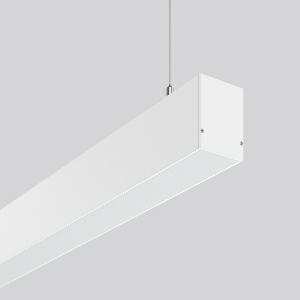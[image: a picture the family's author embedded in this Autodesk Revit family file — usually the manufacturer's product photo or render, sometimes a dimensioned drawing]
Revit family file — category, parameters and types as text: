
# Revit family: less_is_more_50_312318_002_21ed
name_source: partatom
category: Lighting Fixtures
units: mm (PartAtom-declared; Revit-internal decimal feet)

## family parameters
Cut with Voids When Loaded = No
Host = Face
Light Source = No
Part Type = Normal
Room Calculation Point = No
Round Connector Dimension = Use Diameter
Shared = No

## types (1)
- LESS IS MORE 50 (1 x LED Modul 830, 4600 lm, 3000)
    Apparent Load = 40 VA
    CIE Flux Codes = 49 80 96 63 100
    Color Rendering = 80
    Color Temperature = 3000
    Default Elevation = 1800 mm
    Description = Series: LESS IS MORE 50
Linear pendant luminaire for aesthetically sophisticated lighting. Housing: extruded aluminium profile, powder-coated. End cap aluminium powder-coated. Canopy made of aluminium, powder-coated. Diffuser made of non-yellowing plastic (PMMA), opal. Direct 65%, indirect 35% light emission. Suitable for pendant. 2-point steel cable suspension freely positionable and infinitely height-adjustable. Special lengths available on request. LED unit with integrated converter interchangeable and removable. Suitable for through-wiring. With sensors or as a safety luminaire on request. 
Colour: traffic white, matt (RAL 9016)
Length: 1127 mm
Width: 57 mm
Height: 75 mm
Suspension length: 2000 mm
Lamp: LED
Socket: without socket
Colour temperature: 3000K
Colour rendering index (CRI): 80
Light source: LED
Socket lamp2: Without base
Colour temperature: 3000K
System power: 40 W
Rated luminous flux: 4600 lm
Luminous efficiency: 115 lm/W
Control gear: Regulated power supply
Control gear: Regulated power supply
Protection class: I
Type of protection: IP 20
    Height = 75 mm
    Lamp = 1 x LED Modul 830
    Lamp Light Flux = 4600 lm
    Lamp count = 1
    Length = 1127 mm
    Lifetime = 50000 h
    Luminous efficacy = 115 lm/W
    Manufacturer = RZB
    ModVariant = No
    Model = 312318.002
    Mounting Place = Ceiling
    Mounting Type = Pendant
    Number of Poles = 1
    OnlyDefault = Yes
    Power Factor = 1
    Product Name = LESS IS MORE 50
    Product group = Pendant LED linear luminaires
    ProductGroupID = 907
    Protection Class = Protection class I
    Protection Degree = IP 20
    RLX_Detail_Level = 1
    RLX_Emergency_Light_Flux = 0 lm
    RLX_Emergency_Type = 0
    RLX_Emergency_Type_DB = No
    RlxData = <blob elided: 31649 chars, md5=420aada2>
    Socket = socket
    Standby Power = 0 W
    System Light Flux = 4600 lm
    System Power = 40 W
    Type Comments = Product without accessories
    Type Image = 312318.002.jpg
    URL = http://relux.com
    VarID = ---
    Voltage = 230 V
    Voltage Range = 220-240 V
    Weight = 0.00 kg
    Width = 57 mm

## geometry (parser evidence)
native form markers: Blend x4, Sweep x14
no freeform markers — native parametric forms only
